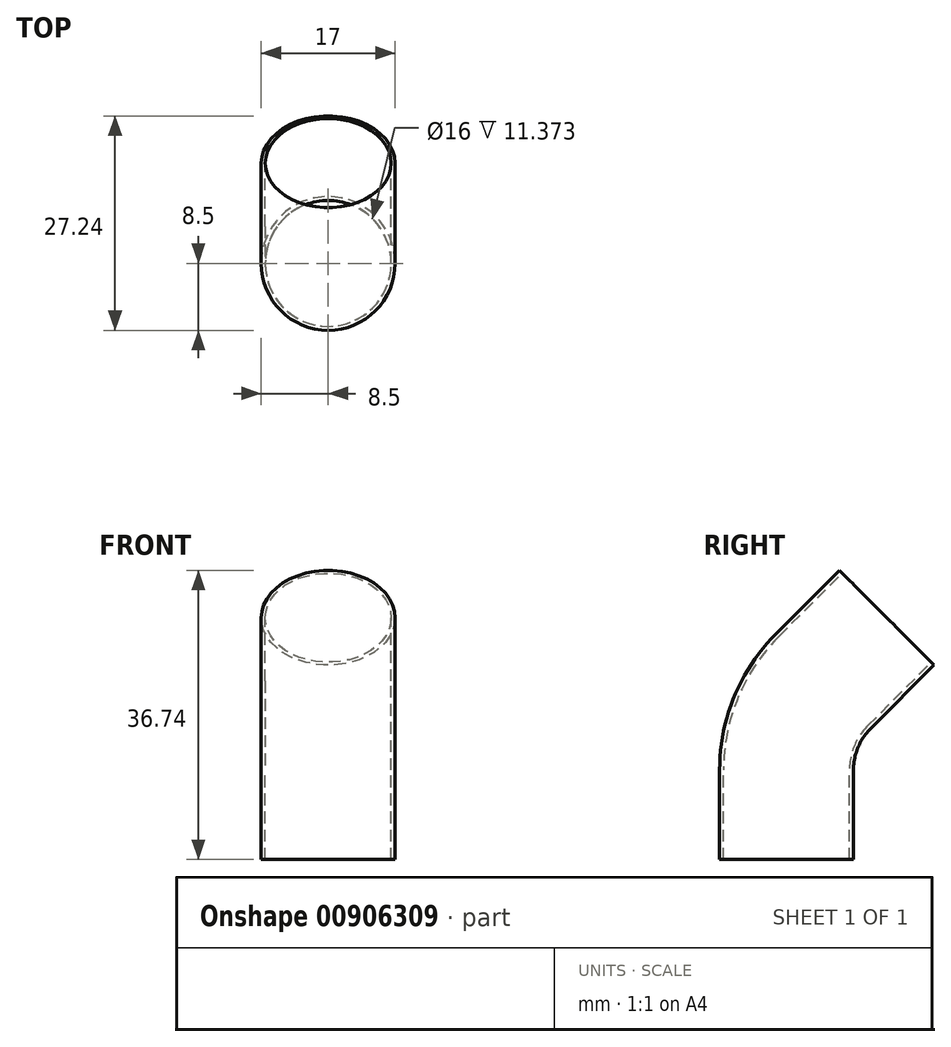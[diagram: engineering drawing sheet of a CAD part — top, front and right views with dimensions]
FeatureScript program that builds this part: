
annotation { "Feature Type Name" : "Feature", "Feature Type Description" : "" }
export const myFeature = defineFeature(function(context is Context, id is Id, definition is map)
    precondition{}
    {
        {
            var Q0;
            Q0=qCreatedBy(makeId("Top.planeOp"),FACE);
            var sketch = newSketch(context, id + "F0", { "sketchPlane" : qUnion([Q0])});
            skCircle(sketch, "E0", {"center": v(0, 0) * mm, "radius": 8.5 * mm});
            skCircle(sketch, "E1", {"center": v(0, 0) * mm, "radius": 8 * mm});
            skSolve(sketch);
        }
        {
            var Q0;
            Q0=qCreatedBy(makeId("Right.planeOp"),FACE);
            var sketch = newSketch(context, id + "F1", { "sketchPlane" : qUnion([Q0])});
            skLineSegment(sketch, "E2", {"start": v(0, 0) * mm, "end": v(0, 11.37) * mm});
            skLineSegment(sketch, "E3", {"start": v(4.69, 22.69) * mm, "end": v(12.73, 30.73) * mm});
            skPoint(sketch, "E4.visualSharp", {"position": v(0, 18) * mm});
            skArc(sketch, "E4.filletArc", {"start": v(4.69, 22.69) * mm, "mid": v(1.22, 17.5) * mm, "end": v(0, 11.37) * mm});
            skSolve(sketch);
        }
        {
            var Q0;
            Q0=makeQuery(id+"F0.imprint","IMPRINT",FACE,{"disambiguationData":[TD([[makeQuery(id+"F0.imprint","IMPRINT",EDGE,{"derivedFrom":sQuery(id+"F0.wireOp",EDGE,"E0")}),1.0]])]});
            var Q1;
            Q1=sQuery(id+"F1.wireOp",EDGE,"E2");
            var Q2;
            Q2=sQuery(id+"F1.wireOp",EDGE,"E4.filletArc");
            var Q3;
            Q3=sQuery(id+"F1.wireOp",EDGE,"E3");
            sweep(context, id + "F2", {"profiles" : qUnion([Q0]), "path" : qUnion([Q1, Q2, Q3])});
        }
    });
